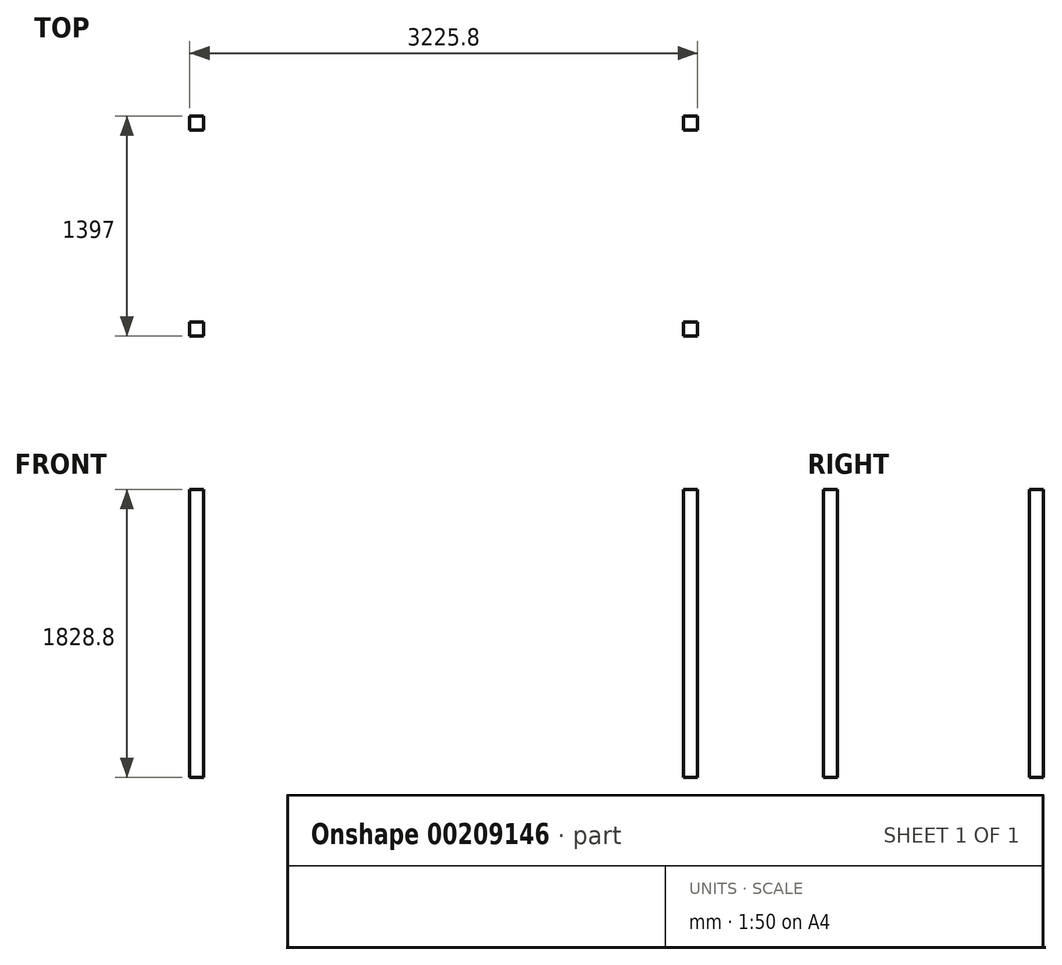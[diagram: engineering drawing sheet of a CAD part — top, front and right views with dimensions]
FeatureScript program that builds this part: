
annotation { "Feature Type Name" : "Feature", "Feature Type Description" : "" }
export const myFeature = defineFeature(function(context is Context, id is Id, definition is map)
    precondition{}
    {
        {
            var Q0;
            Q0=qCreatedBy(makeId("Top.planeOp"),FACE);
            var sketch = newSketch(context, id + "F0", { "sketchPlane" : qUnion([Q0])});
            skLineSegment(sketch, "E0.bottom", {"start": v(44.45, 698.5) * mm, "end": v(-44.45, 698.5) * mm});
            skLineSegment(sketch, "E0.top", {"start": v(44.45, 609.6) * mm, "end": v(-44.45, 609.6) * mm});
            skLineSegment(sketch, "E0.left", {"start": v(44.45, 698.5) * mm, "end": v(44.45, 609.6) * mm});
            skLineSegment(sketch, "E0.right", {"start": v(-44.45, 698.5) * mm, "end": v(-44.45, 609.6) * mm});
            skPoint(sketch, "E0.middle", {"position": v(0, 654.05) * mm});
            skLineSegment(sketch, "E1.bottom", {"start": v(44.45, -609.6) * mm, "end": v(-44.45, -609.6) * mm});
            skLineSegment(sketch, "E1.top", {"start": v(44.45, -698.5) * mm, "end": v(-44.45, -698.5) * mm});
            skLineSegment(sketch, "E1.left", {"start": v(44.45, -609.6) * mm, "end": v(44.45, -698.5) * mm});
            skLineSegment(sketch, "E1.right", {"start": v(-44.45, -609.6) * mm, "end": v(-44.45, -698.5) * mm});
            skPoint(sketch, "E1.middle", {"position": v(0, -654.05) * mm});
            skLineSegment(sketch, "E2", {"start": v(0, 609.6) * mm, "end": v(0, 0) * mm});
            skLineSegment(sketch, "E3", {"start": v(0, 0) * mm, "end": v(0, -609.6) * mm});
            skLineSegment(sketch, "E4.bottom", {"start": v(-3092.45, 698.5) * mm, "end": v(-3181.35, 698.5) * mm});
            skLineSegment(sketch, "E4.top", {"start": v(-3092.45, 609.6) * mm, "end": v(-3181.35, 609.6) * mm});
            skLineSegment(sketch, "E4.left", {"start": v(-3092.45, 698.5) * mm, "end": v(-3092.45, 609.6) * mm});
            skLineSegment(sketch, "E4.right", {"start": v(-3181.35, 698.5) * mm, "end": v(-3181.35, 609.6) * mm});
            skPoint(sketch, "E4.middle", {"position": v(-3136.9, 654.05) * mm});
            skLineSegment(sketch, "E5.bottom", {"start": v(-3092.45, -609.6) * mm, "end": v(-3181.35, -609.6) * mm});
            skLineSegment(sketch, "E5.top", {"start": v(-3092.45, -698.5) * mm, "end": v(-3181.35, -698.5) * mm});
            skLineSegment(sketch, "E5.left", {"start": v(-3092.45, -609.6) * mm, "end": v(-3092.45, -698.5) * mm});
            skLineSegment(sketch, "E5.right", {"start": v(-3181.35, -609.6) * mm, "end": v(-3181.35, -698.5) * mm});
            skPoint(sketch, "E5.middle", {"position": v(-3136.9, -654.05) * mm});
            skSolve(sketch);
        }
        {
            var Q0;
            Q0 = qSketchRegion(id + "F0", true);
            extrude(context, id + "F1", {"entities" : qUnion([Q0]), "depth" : 1828.8 * mm});
        }
    });
